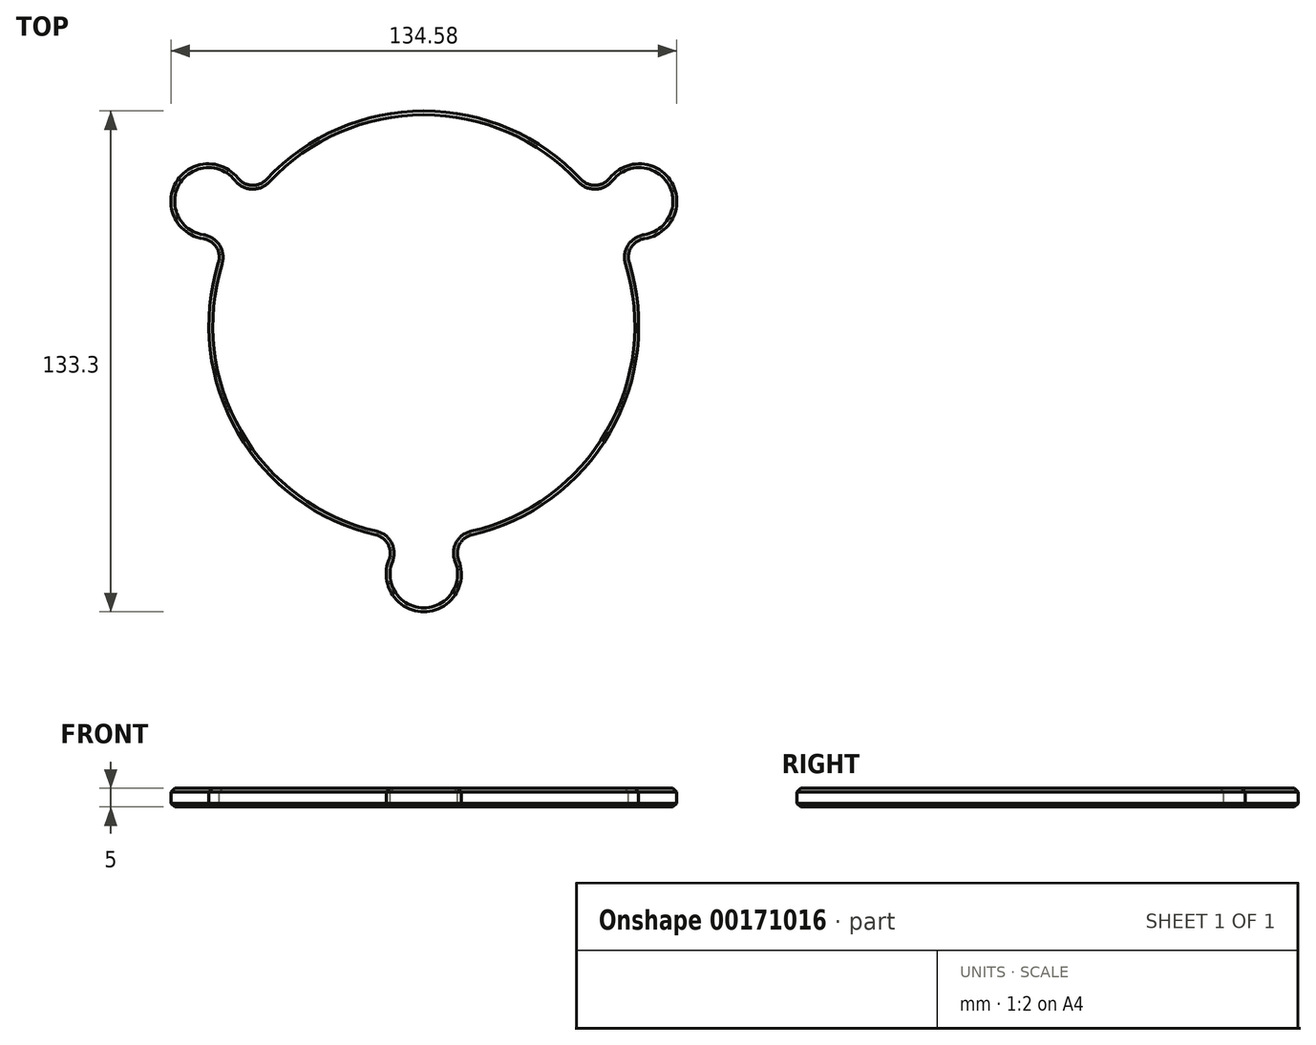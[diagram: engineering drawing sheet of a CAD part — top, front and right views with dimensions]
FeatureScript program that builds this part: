
annotation { "Feature Type Name" : "Feature", "Feature Type Description" : "" }
export const myFeature = defineFeature(function(context is Context, id is Id, definition is map)
    precondition{}
    {
        {
            var Q0;
            Q0=qCreatedBy(makeId("Top.planeOp"),FACE);
            var sketch = newSketch(context, id + "F0", { "sketchPlane" : qUnion([Q0])});
            skCircle(sketch, "E0", {"center": v(0, 0) * mm, "radius": 57.15 * mm});
            skArc(sketch, "E1", {"start": v(-4.05, -57) * mm, "mid": v(0, -76.15) * mm, "end": v(4.05, -57) * mm});
            skArc(sketch, "E2.1.0", {"start": v(51.4, 25) * mm, "mid": v(65.95, 38.07) * mm, "end": v(47.34, 32) * mm});
            skArc(sketch, "E2.2.0", {"start": v(-47.34, 32) * mm, "mid": v(-65.95, 38.08) * mm, "end": v(-51.4, 25) * mm});
            skSolve(sketch);
        }
        {
            var Q0;
            {var subQ0=sQuery(id+"F0.wireOp",EDGE,"E2.2.0");Q0=makeQuery(id+"F0.imprint","IMPRINT",FACE,{"disambiguationData":[TD([[makeQuery(id+"F0.imprint","IMPRINT",EDGE,{"derivedFrom":subQ0}),1.0]])]});}
            var Q1;
            {var subQ0=sQuery(id+"F0.wireOp",EDGE,"E2.1.0");Q1=makeQuery(id+"F0.imprint","IMPRINT",FACE,{"disambiguationData":[TD([[makeQuery(id+"F0.imprint","IMPRINT",EDGE,{"derivedFrom":subQ0}),1.0]])]});}
            var Q2;
            {var subQ1=sQuery(id+"F0.wireOp",EDGE,"E0");var subQ6=sQuery(id+"F0.wireOp",EDGE,"E2.1.0");var subQ8=makeQuery(id+"F0.imprint","INTERSECT",VERTEX,{"disambiguationData":[OD(0.0)],"derivedFrom":[subQ1,subQ6]});Q2=makeQuery(id+"F0.imprint","IMPRINT",FACE,{"disambiguationData":[TD([[makeQuery(id+"F0.imprint","IMPRINT",EDGE,{"disambiguationData":[TD([[subQ8,-1.0]])],"derivedFrom":subQ1}),1.0]])]});}
            var Q3;
            {var subQ0=sQuery(id+"F0.wireOp",EDGE,"E1");Q3=makeQuery(id+"F0.imprint","IMPRINT",FACE,{"disambiguationData":[TD([[makeQuery(id+"F0.imprint","IMPRINT",EDGE,{"derivedFrom":subQ0}),1.0]])]});}
            extrude(context, id + "F1", {"entities" : qUnion([Q0, Q1, Q2, Q3]), "depth" : 5 * mm});
        }
        {
            var Q0;
            {var subQ0=sQuery(id+"F0.wireOp",EDGE,"E1");var subQ1=sQuery(id+"F0.wireOp",EDGE,"E0");Q0=makeQuery(id+"F1.opExtrude","SWEPT_EDGE",EDGE,{"disambiguationData":[OSD([subQ1,subQ0]),TDD([makeQuery(id+"F0.imprint","INTERSECT",VERTEX,{"disambiguationData":[OD(1.0)],"derivedFrom":[subQ1,subQ0]})])]});}
            var Q1;
            {var subQ0=sQuery(id+"F0.wireOp",EDGE,"E1");var subQ1=sQuery(id+"F0.wireOp",EDGE,"E0");Q1=makeQuery(id+"F1.opExtrude","SWEPT_EDGE",EDGE,{"disambiguationData":[OSD([subQ1,subQ0]),TDD([makeQuery(id+"F0.imprint","INTERSECT",VERTEX,{"disambiguationData":[OD(0.0)],"derivedFrom":[subQ1,subQ0]})])]});}
            var Q2;
            {var subQ0=sQuery(id+"F0.wireOp",EDGE,"E2.2.0");var subQ1=sQuery(id+"F0.wireOp",EDGE,"E0");Q2=makeQuery(id+"F1.opExtrude","SWEPT_EDGE",EDGE,{"disambiguationData":[OSD([subQ1,subQ0]),TDD([makeQuery(id+"F0.imprint","INTERSECT",VERTEX,{"disambiguationData":[OD(1.0)],"derivedFrom":[subQ1,subQ0]})])]});}
            var Q3;
            {var subQ0=sQuery(id+"F0.wireOp",EDGE,"E2.2.0");var subQ1=sQuery(id+"F0.wireOp",EDGE,"E0");Q3=makeQuery(id+"F1.opExtrude","SWEPT_EDGE",EDGE,{"disambiguationData":[OSD([subQ1,subQ0]),TDD([makeQuery(id+"F0.imprint","INTERSECT",VERTEX,{"disambiguationData":[OD(0.0)],"derivedFrom":[subQ1,subQ0]})])]});}
            var Q4;
            {var subQ0=sQuery(id+"F0.wireOp",EDGE,"E2.1.0");var subQ1=sQuery(id+"F0.wireOp",EDGE,"E0");Q4=makeQuery(id+"F1.opExtrude","SWEPT_EDGE",EDGE,{"disambiguationData":[OSD([subQ1,subQ0]),TDD([makeQuery(id+"F0.imprint","INTERSECT",VERTEX,{"disambiguationData":[OD(1.0)],"derivedFrom":[subQ1,subQ0]})])]});}
            var Q5;
            {var subQ0=sQuery(id+"F0.wireOp",EDGE,"E2.1.0");var subQ1=sQuery(id+"F0.wireOp",EDGE,"E0");Q5=makeQuery(id+"F1.opExtrude","SWEPT_EDGE",EDGE,{"disambiguationData":[OSD([subQ1,subQ0]),TDD([makeQuery(id+"F0.imprint","INTERSECT",VERTEX,{"disambiguationData":[OD(0.0)],"derivedFrom":[subQ1,subQ0]})])]});}
            fillet(context, id + "F2", {"entities" : qUnion([Q0, Q1, Q2, Q3, Q4, Q5]), "radius" : 5 * mm, "tangentPropagation" : true, "allowEdgeOverflow" : false});
        }
        {
            var Q0;
            Q0=makeQuery(id+"F1.opExtrude","CAP_FACE",FACE,{"disambiguationData":[OSD([sQuery(id+"F0.wireOp",EDGE,"E0"),sQuery(id+"F0.wireOp",EDGE,"E1"),sQuery(id+"F0.wireOp",EDGE,"E2.1.0"),sQuery(id+"F0.wireOp",EDGE,"E2.2.0")])],"isStart":true});
            var Q1;
            Q1=makeQuery(id+"F1.opExtrude","CAP_FACE",FACE,{"disambiguationData":[OSD([sQuery(id+"F0.wireOp",EDGE,"E0"),sQuery(id+"F0.wireOp",EDGE,"E1"),sQuery(id+"F0.wireOp",EDGE,"E2.1.0"),sQuery(id+"F0.wireOp",EDGE,"E2.2.0")])],"isStart":false});
            chamfer(context, id + "F3", {"entities" : qUnion([Q0, Q1]), "width" : 1 * mm, "tangentPropagation" : true});
        }
    });
